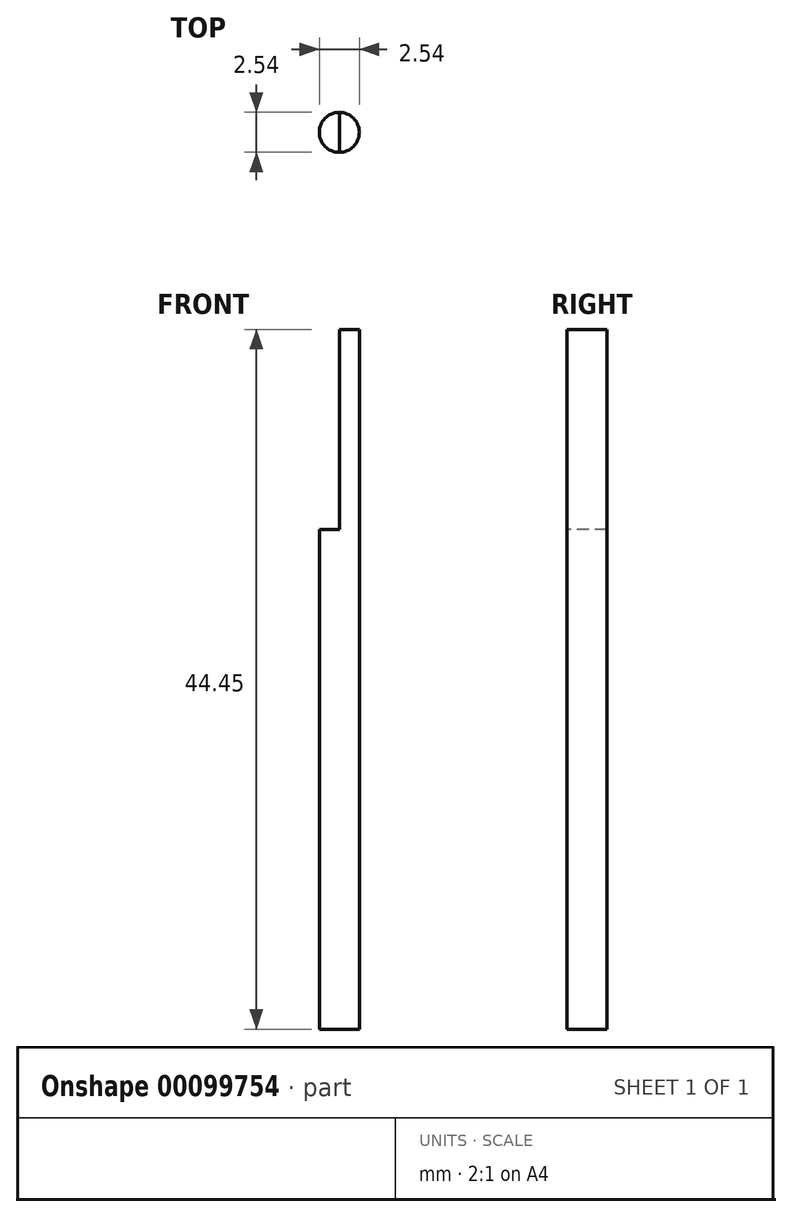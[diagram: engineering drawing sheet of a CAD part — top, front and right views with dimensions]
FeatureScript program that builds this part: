
annotation { "Feature Type Name" : "Feature", "Feature Type Description" : "" }
export const myFeature = defineFeature(function(context is Context, id is Id, definition is map)
    precondition{}
    {
        {
            var Q0;
            Q0=qCreatedBy(makeId("Top.planeOp"),FACE);
            var sketch = newSketch(context, id + "F0", { "sketchPlane" : qUnion([Q0])});
            skCircle(sketch, "E0", {"center": v(0, 0) * mm, "radius": 1.27 * mm});
            skSolve(sketch);
        }
        {
            var Q0;
            Q0=makeQuery(id+"F0.imprint","IMPRINT",FACE,{"disambiguationData":[TD([[makeQuery(id+"F0.imprint","IMPRINT",EDGE,{"derivedFrom":sQuery(id+"F0.wireOp",EDGE,"E0")}),1.0]])]});
            extrude(context, id + "F1", {"entities" : qUnion([Q0]), "depth" : 44.45 * mm});
        }
        {
            var Q0;
            Q0=makeQuery(id+"F1.opExtrude","CAP_FACE",FACE,{"disambiguationData":[OSD([sQuery(id+"F0.wireOp",EDGE,"E0")])],"isStart":false});
            var sketch = newSketch(context, id + "F2", { "sketchPlane" : qUnion([Q0])});
            skArc(sketch, "E1", {"start": v(0, 1.27) * mm, "mid": v(-1.27, 0) * mm, "end": v(0, -1.27) * mm});
            skLineSegment(sketch, "E2", {"start": v(0, 1.27) * mm, "end": v(0, -1.27) * mm});
            skSolve(sketch);
        }
        {
            var Q0;
            Q0=makeQuery(id+"F2.imprint","IMPRINT",FACE,{"disambiguationData":[TD([[makeQuery(id+"F2.imprint","IMPRINT",EDGE,{"derivedFrom":sQuery(id+"F2.wireOp",EDGE,"E1")}),1.0]])]});
            extrude(context, id + "F3", {"entities" : qUnion([Q0]), "operationType" : NewBodyOperationType.REMOVE, "oppositeDirection" : true, "depth" : 12.7 * mm});
        }
    });
